# Revit family: Shower-Handshower_Kit-KOHLER-PURIST-K-72636T_1
name_source: partatom
category: Plumbing Fixtures
revit_build: Autodesk Revit 2017 (Build: 20160225_1515(x64)
units: mm (PartAtom-declared; Revit-internal decimal feet)

## family parameters
Cut with Voids When Loaded = No
Host = Face
OmniClass Number = 23.31.17.00
OmniClass Title = Showers
Part Type = Normal
Room Calculation Point = No
Round Connector Dimension = Use Diameter
Shared = No

## types (3) — shared parameters
ADA Compliant = No
Assembly Code = D2010700
CW Connection = Yes
Cold Water Inlet = Cold Water Inlet
Date Modified = 15/09/2020
Default Elevation = 0"
Description = Cylinder side water divider and hand shower
Drain Included = No
Flow Rate = 3 GPM
HW Connection = Yes
Height = 10 7/8"
Hot Water Inlet = Hot Water Inlet
Length = 3 1/16"
Manufacturer = KOHLER Co.
Master Format 2014 = 22 42 23
Master Format 2014 Name = Residential Showers
Material = Premium Metal Construction
Pressure = 80.00 psi
Product Documentation Link = https://files.kohler.com.cn
Product Name = PURIST
Product Page URL = https://www.kohler.com.cn
URL = http://www.kohler.com.cn
Vent Connection = No
Waste Connection = No
Waste Water Outlet = Waste Water Outlet
WaterSense Certified = No
Width = 4 13/16"

## per-type parameters (varying)
| type | Cross Handle | Dist 1 | Dist 2 | Finish | Handle Clearance | Handle Height | Lever Handle | Model | Type |
| Lever Handle, RGD-Rose Gold | No | 0" | 1 3/8" | Kohler-Metal-RGD-Rose_Gold | 2 5/8" | 4 3/4" | Yes | K-72636T-4-RGD | 3 |
| Cross Handel, RGD-Rose Gold | Yes | 1 3/4" | 0" | Kohler-Metal-RGD-Rose_Gold | 3 1/2" | 4 11/16" | No | K-72636T-3-RGD | 2 |
| Cross Handel, CP-Polished Chrome | Yes | 1 3/4" | 0" | Kohler-Metal-CP-Polished_Chrome | 3 1/2" | 4 11/16" | No | K-72636T-3-CP | 1 |

## geometry (parser evidence)
native form markers: Sweep x7
no freeform markers — native parametric forms only
